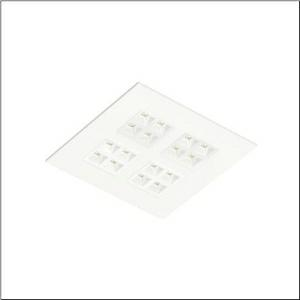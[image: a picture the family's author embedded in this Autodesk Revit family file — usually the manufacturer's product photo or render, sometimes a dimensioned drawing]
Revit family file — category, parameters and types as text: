
# Revit family: silica_31_square_51my6nds44wa
name_source: partatom
category: Lighting Fixtures
units: mm (PartAtom-declared; Revit-internal decimal feet)

## family parameters
Cut with Voids When Loaded = No
Host = Face
Light Source = No
Part Type = Normal
Room Calculation Point = No
Round Connector Dimension = Use Diameter
Shared = No

## types (1)
- --- (1 x LED, 6640 lm, 38.5 W, 4000K)
    Apparent Load = 39 VA
    CIE Flux Codes = 81 99 100 100 100
    Color Rendering = 80
    Color Temperature = 4000K
    Default Elevation = 1800 mm
    Description = Silica 31 Square, office luminaire, primary light control with lens, of PMMA, primary anti-glare with reflector, of PC, white, light emission: direct distribution, primary light characteristic: symmetric, installation type: lay-in mounting, LED, rated luminous flux: 4.570lm, luminous efficacy: 176lm/W, light colour: 840, colour temperature: 4000K, control gear: DALI 2, Multilumen, with terminal, 5-pole, mains connection: 220..240V, AC, 50/60Hz, rated input power: 26W, luminaire housing, of sheet steel, coated, traffic white (RAL 9016), module: M600, length: 595mm, width: 595mm, height: 43mm, protection rating (complete): IP20, insulation class (complete): insulation class II (safety insulation), certification: CE, impact resistance: IK03, permissible operating ambient temperature: -20..+35°C, standard: EN 50419, packaging unit: 1 piece
    Height = 0 mm  [stored 0 ft]
    Lamp = 1 x LED
    Lamp Light Flux = 6640 lm
    Lamp Power = 38.5 W
    Lamp count = 1
    Length = 595 mm
    Luminous efficacy = 172 lm/W
    Manufacturer = Siteco
    ModVariant = No
    Model = 51MY6NDS44WA
    Mounting Place = Ceiling
    Mounting Type = Recessed
    Number of Poles = 1
    OnlyDefault = Yes
    Power Factor = 1
    Product Name = Silica 31 Square
    Product group = office luminaire | ceiling recessed
    ProductGroupID = 400
    Protection Class = Protection class II
    Protection Degree = IP 20
    RLX_Detail_Level = 1
    RLX_Emergency_Light_Flux = 0 lm
    RLX_Emergency_Type = 0
    RLX_Emergency_Type_DB = No
    RlxData = <blob elided: 27885 chars, md5=a1f66631>
    Socket = socket
    Standby Power = 0 W
    System Light Flux = 6640 lm
    System Power = 39 W
    Type Comments = factory setting: luminous flux: 100 % | (OFF | OFF | OFF | OFF) | 1050 mA
    Type Image = l_1313651.jpg
    URL = http://relux.com
    VarID = @adj_043045
    Voltage = 0 V
    Weight = 0.00 kg
    Width = 595 mm

note: [stored X ft] marks values corroborated as IEEE doubles in the binary element streams (Revit-internal decimal feet)

## geometry (parser evidence)
native form markers: Blend x4, Sweep x11
no freeform markers — native parametric forms only
